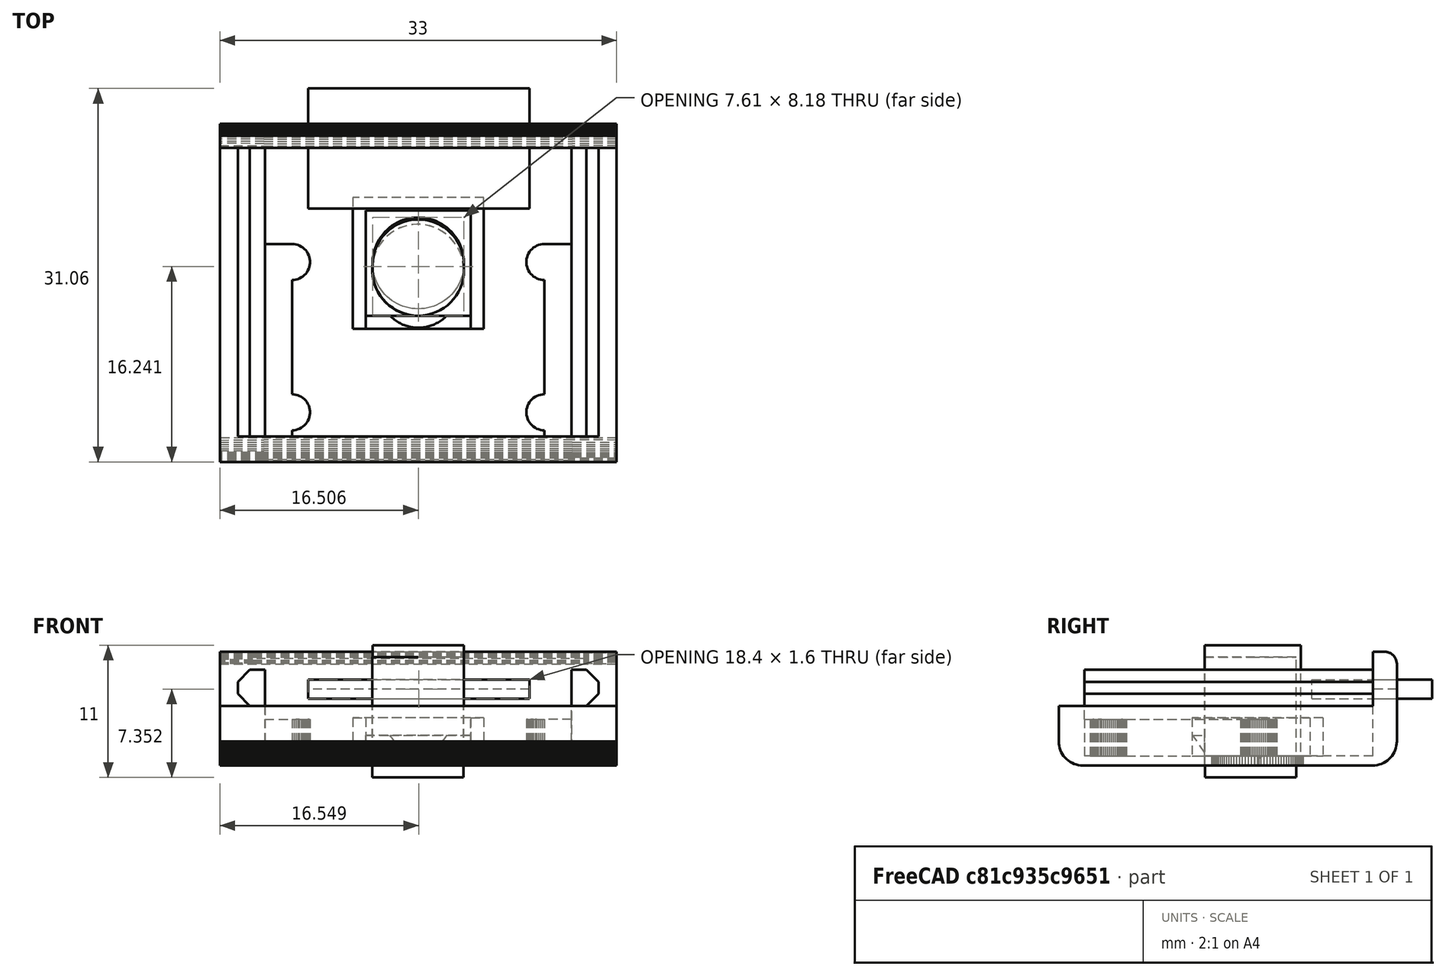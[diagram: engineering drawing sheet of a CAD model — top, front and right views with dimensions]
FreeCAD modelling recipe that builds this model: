
FCSTD DOCUMENT  (FreeCAD 0.18.3R)
Label: PiCam Mount
License: All rights reserved
LicenseURL: http://en.wikipedia.org/wiki/All_rights_reserved
objects: Part::FeaturePython×6, Part::Feature×4, Part::Box×2, Part::Cylinder×1, Mesh::Feature×1, Part::Fillet×1, Part::Cut×1, App::DocumentObjectGroup×1
note: 15 computed .brp shape members not serialized (recipe doc carries the construction recipe); baked Part::Feature solids carry a one-line shape summary decoded from their .brp

FEATURE [Part::Cylinder] Cylinder
  Angle = 360
  AttacherType = Attacher::AttachEngine3D
  Height = 10
  Placement = pos=(114.97,116.9,-1) rot=(0,0,1;0rad)
  Radius = 3.8
FEATURE [Mesh::Feature] Picam_2_Front_Housing
FEATURE [Part::Feature] Picam_2_Front_Housing001
  shape: bbox 33 x 28.13 x 9.452 mm, 1962 faces, 0 solids (baked)
FEATURE [Part::Box] Box  label="Cube"
  AttacherType = Attacher::AttachEngine3D
  Height = 1.6
  Length = 18.4
  Placement = pos=(105.849,122,5.552) rot=(0,0,1;0rad)
  Width = 10
FEATURE [Part::Box] Box001  label="Cube001"
  AttacherType = Attacher::AttachEngine3D
  Height = 10
  Length = 7.6
  Placement = pos=(111.21,113.093,0) rot=(0,0,1;0rad)
  Width = 8
FEATURE [Part::Fillet] Fillet
  Base = -> Box001
  Edges = 4 edges r=3.79: [Edge1,Edge3,Edge5,Edge7]
FEATURE [Part::Feature] Picam_2_Front_Housing001001  label="Picam_2_Front_Housing002"
  shape: bbox 33 x 28.13 x 9.452 mm, 466 faces, 0 solids (baked)
FEATURE [Part::Feature] Solid
  shape: bbox 33 x 28.13 x 9.452 mm, 466 faces (baked)
FEATURE [Part::FeaturePython] Slice  # WARN: FeaturePython — macro-defined, semantics opaque (R4)
  Base = -> Solid
  Mode = 1
  Tolerance = 0
  Tools = -> [Box,Fillet]
FEATURE [Part::FeaturePython] Slice_child0  label="Slice.0"  # WARN: FeaturePython — macro-defined, semantics opaque (R4)
  Base = -> Slice
  FilterType = 1
  Invert = false
  OverrideMaxVal = 0
  WindowFrom = 80
  WindowTo = 100
  items = 0
FEATURE [Part::FeaturePython] Slice_child1  label="Slice.1"  # WARN: FeaturePython — macro-defined, semantics opaque (R4)
  Base = -> Slice
  FilterType = 1
  Invert = false
  OverrideMaxVal = 0
  WindowFrom = 80
  WindowTo = 100
  items = 1
FEATURE [Part::FeaturePython] Slice_child2  label="Slice.2"  # WARN: FeaturePython — macro-defined, semantics opaque (R4)
  Base = -> Slice
  FilterType = 1
  Invert = false
  OverrideMaxVal = 0
  WindowFrom = 80
  WindowTo = 100
  items = 2
FEATURE [Part::FeaturePython] Slice_child3  label="Slice.3"  # WARN: FeaturePython — macro-defined, semantics opaque (R4)
  Base = -> Slice
  FilterType = 1
  Invert = false
  OverrideMaxVal = 0
  Placement = pos=(0,0,-0.799997) rot=(0,0,1;0rad)
  WindowFrom = 80
  WindowTo = 100
  items = 3
FEATURE [Part::Feature] Fillet001
  Placement = pos=(0,22.1521,-66.2231) rot=(1,0,0;0.610865rad)
  shape: bbox 7.6 x 12.29 x 12.78 mm, 10 faces (baked)
FEATURE [Part::Cut] Cut
  Base = -> Slice_child0
  Tool = -> Fillet001
FEATURE [App::DocumentObjectGroup] GrExplode_Slice  label="Exploded Slice"
  Group = -> [Slice_child1,Slice_child2,Slice_child3,Cut]
FEATURE [Part::FeaturePython] Connect  # WARN: FeaturePython — macro-defined, semantics opaque (R4)
  Objects = -> [Slice_child3,Cut]
  Tolerance = 0
